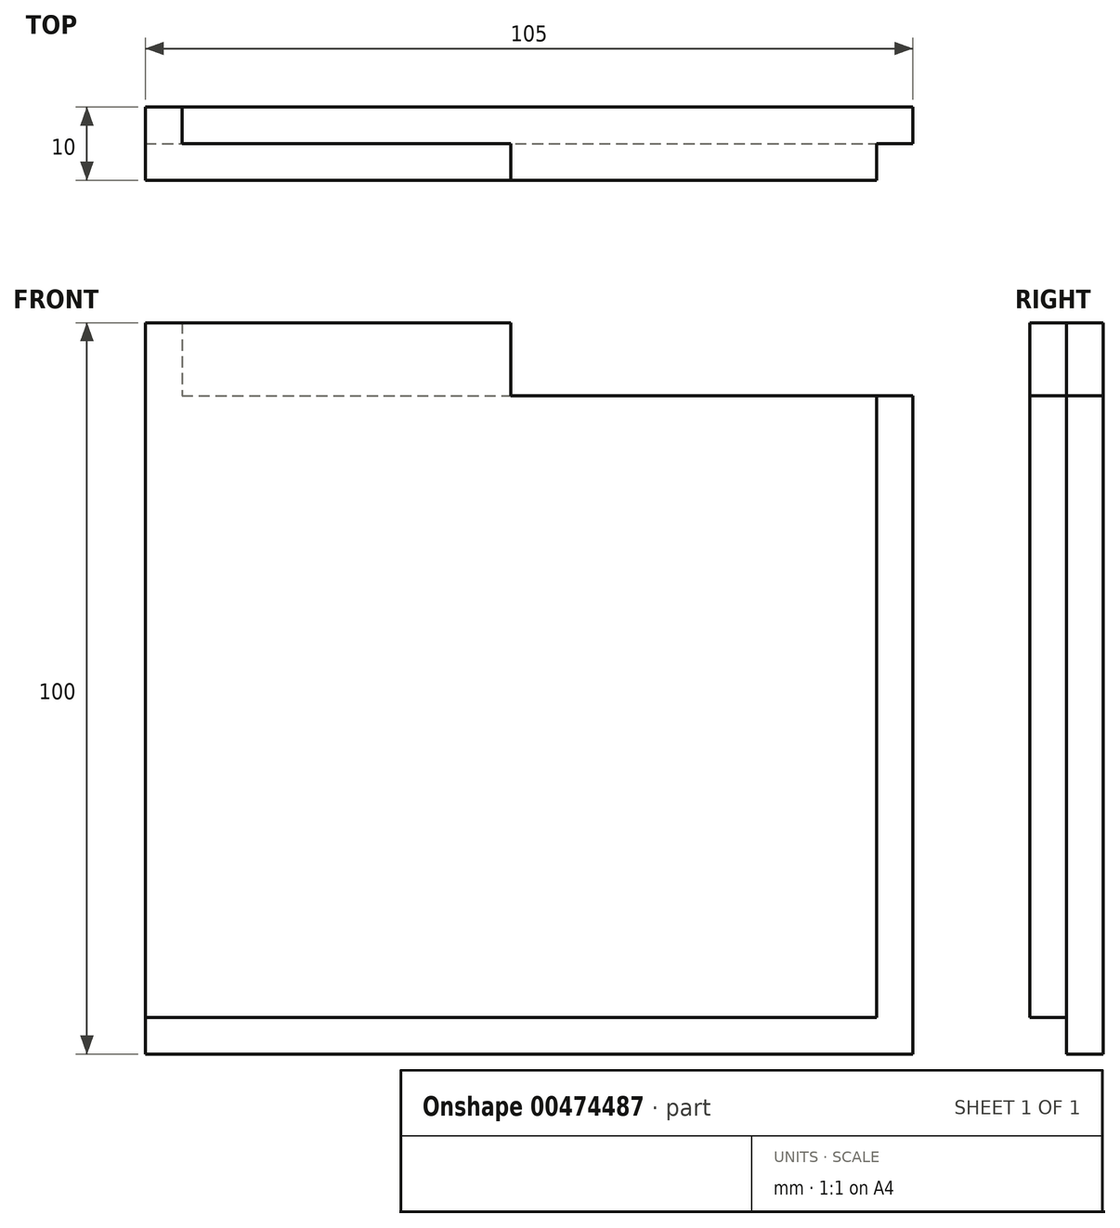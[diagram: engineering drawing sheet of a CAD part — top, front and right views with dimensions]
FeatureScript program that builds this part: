
annotation { "Feature Type Name" : "Feature", "Feature Type Description" : "" }
export const myFeature = defineFeature(function(context is Context, id is Id, definition is map)
    precondition{}
    {
        {
            var Q0;
            Q0=qCreatedBy(makeId("Front.planeOp"),FACE);
            var sketch = newSketch(context, id + "F0", { "sketchPlane" : qUnion([Q0])});
            skLineSegment(sketch, "E0.bottom", {"start": v(-52.5, 47.5) * mm, "end": v(52.5, 47.5) * mm});
            skLineSegment(sketch, "E0.top", {"start": v(-52.5, -47.5) * mm, "end": v(52.5, -47.5) * mm});
            skLineSegment(sketch, "E0.left", {"start": v(-52.5, 47.5) * mm, "end": v(-52.5, -47.5) * mm});
            skLineSegment(sketch, "E0.right", {"start": v(52.5, 47.5) * mm, "end": v(52.5, -47.5) * mm});
            skPoint(sketch, "E0.middle", {"position": v(0, 0) * mm});
            skSolve(sketch);
        }
        {
            var Q0;
            Q0 = qSketchRegion(id + "F0", true);
            var Q1;
            Q1=makeQuery(id+"F0.imprint","IMPRINT",FACE,{"disambiguationData":[TD([[makeQuery(id+"F0.imprint","IMPRINT",EDGE,{"derivedFrom":sQuery(id+"F0.wireOp",EDGE,"E0.bottom")}),-1.0]])]});
            extrude(context, id + "F1", {"entities" : qUnion([Q0, Q1]), "depth" : 5 * mm});
        }
        {
            var Q0;
            Q0=makeQuery(id+"F1.opExtrude","SWEPT_FACE",FACE,{"disambiguationData":[OSD([sQuery(id+"F0.wireOp",EDGE,"E0.bottom")])]});
            var sketch = newSketch(context, id + "F2", { "sketchPlane" : qUnion([Q0])});
            skLineSegment(sketch, "E1", {"start": v(-2.5, 0) * mm, "end": v(-2.5, -5) * mm});
            skSolve(sketch);
        }
        {
            var Q0;
            {var subQ0=sQuery(id+"F2.wireOp",EDGE,"E1");Q0=makeQuery(id+"F2.imprint","IMPRINT",FACE,{"disambiguationData":[TD([[makeQuery(id+"F2.imprint","IMPRINT",EDGE,{"derivedFrom":subQ0}),-1.0]])]});}
            extrude(context, id + "F3", {"entities" : qUnion([Q0]), "operationType" : NewBodyOperationType.ADD, "depth" : 5 * mm});
        }
        {
            var Q0;
            {var subQ0=sQuery(id+"F0.wireOp",EDGE,"E0.bottom");var subQ1=makeQuery(id+"F1.opExtrude","CAP_EDGE",EDGE,{"disambiguationData":[OSD([subQ0])],"isStart":false});var subQ2=sQuery(id+"F0.wireOp",EDGE,"E0.left");Q0=makeQuery(id+"F3.boolean.opBoolean","MERGE",FACE,{"derivedFrom":[makeQuery(id+"F1.opExtrude","CAP_FACE",FACE,{"disambiguationData":[OSD([subQ0,sQuery(id+"F0.wireOp",EDGE,"E0.top"),subQ2,sQuery(id+"F0.wireOp",EDGE,"E0.right")])],"isStart":false}),makeQuery(id+"F3.opExtrude","SWEPT_FACE",FACE,{"disambiguationData":[OSD([subQ0]),TDD([makeQuery(id+"F2.imprint","IMPRINT",EDGE,{"disambiguationData":[TD([[makeQuery(id+"F2.imprint","INTERSECT",VERTEX,{"derivedFrom":[subQ1,sQuery(id+"F2.wireOp",EDGE,"E1")]}),1.0]])],"derivedFrom":subQ1})])]})]});}
            var sketch = newSketch(context, id + "F4", { "sketchPlane" : qUnion([Q0])});
            skLineSegment(sketch, "E2", {"start": v(-2.5, 47.5) * mm, "end": v(-2.5, 42.5) * mm});
            skLineSegment(sketch, "E3", {"start": v(-2.5, 42.5) * mm, "end": v(47.5, 42.5) * mm});
            skLineSegment(sketch, "E4", {"start": v(47.5, 42.5) * mm, "end": v(47.5, -42.5) * mm});
            skLineSegment(sketch, "E5", {"start": v(47.5, -42.5) * mm, "end": v(-52.5, -42.5) * mm});
            skSolve(sketch);
        }
        {
            var Q0;
            Q0=makeQuery(id+"F4.imprint","IMPRINT",FACE,{"disambiguationData":[TD([[makeQuery(id+"F4.imprint","IMPRINT",EDGE,{"derivedFrom":sQuery(id+"F4.wireOp",EDGE,"E2")}),-1.0]])]});
            extrude(context, id + "F5", {"entities" : qUnion([Q0]), "operationType" : NewBodyOperationType.ADD, "depth" : 5 * mm});
        }
        {
            var Q0;
            {var subQ0=sQuery(id+"F2.wireOp",EDGE,"E1");Q0=makeQuery(id+"F5.boolean.opBoolean","MERGE",FACE,{"derivedFrom":[makeQuery(id+"F3.opExtrude","SWEPT_FACE",FACE,{"disambiguationData":[OSD([subQ0])]}),makeQuery(id+"F5.opExtrude","SWEPT_FACE",FACE,{"disambiguationData":[OSD([sQuery(id+"F0.wireOp",EDGE,"E0.bottom"),subQ0,sQuery(id+"F4.wireOp",EDGE,"E2")])]})]});}
            var sketch = newSketch(context, id + "F6", { "sketchPlane" : qUnion([Q0])});
            skLineSegment(sketch, "E6", {"start": v(-5, 52.5) * mm, "end": v(-5, 47.5) * mm});
            skSolve(sketch);
        }
        {
            var Q0;
            {var subQ0=sQuery(id+"F6.wireOp",EDGE,"E6");Q0=makeQuery(id+"F6.imprint","IMPRINT",FACE,{"disambiguationData":[TD([[makeQuery(id+"F6.imprint","IMPRINT",EDGE,{"derivedFrom":subQ0}),1.0]])]});}
            extrude(context, id + "F7", {"entities" : qUnion([Q0]), "operationType" : NewBodyOperationType.REMOVE, "oppositeDirection" : true, "depth" : 45 * mm});
        }
        {
            var Q0;
            Q0=makeQuery(id+"F7.boolean.opBoolean","MERGE",FACE,{"derivedFrom":[makeQuery(id+"F1.opExtrude","SWEPT_FACE",FACE,{"disambiguationData":[OSD([sQuery(id+"F0.wireOp",EDGE,"E0.bottom")])]}),makeQuery(id+"F7.opExtrude","SWEPT_FACE",FACE,{"disambiguationData":[OSD([sQuery(id+"F2.wireOp",EDGE,"E1")])]})]});
            var sketch = newSketch(context, id + "F8", { "sketchPlane" : qUnion([Q0])});
            skLineSegment(sketch, "E7", {"start": v(-47.5, 0) * mm, "end": v(-37.5, 0) * mm});
            skLineSegment(sketch, "E8", {"start": v(-37.5, 0) * mm, "end": v(-37.5, -5) * mm});
            skSolve(sketch);
        }
        {
            var Q0;
            Q0=makeQuery(id+"F8.imprint","IMPRINT",FACE,{"disambiguationData":[TD([[makeQuery(id+"F8.imprint","IMPRINT",EDGE,{"derivedFrom":sQuery(id+"F8.wireOp",EDGE,"E7")}),-1.0]])]});
            extrude(context, id + "F9", {"entities" : qUnion([Q0]), "operationType" : NewBodyOperationType.REMOVE, "oppositeDirection" : true, "depth" : 5 * mm});
        }
        {
            var Q0;
            Q0=makeQuery(id+"F9.boolean.opBoolean","COPY",FACE,{"derivedFrom":makeQuery(id+"F9.opExtrude","SWEPT_FACE",FACE,{"disambiguationData":[OSD([sQuery(id+"F8.wireOp",EDGE,"E8")])]})});
            extrude(context, id + "F10", {"entities" : qUnion([Q0]), "operationType" : NewBodyOperationType.REMOVE, "oppositeDirection" : true, "depth" : 90 * mm});
        }
    });
